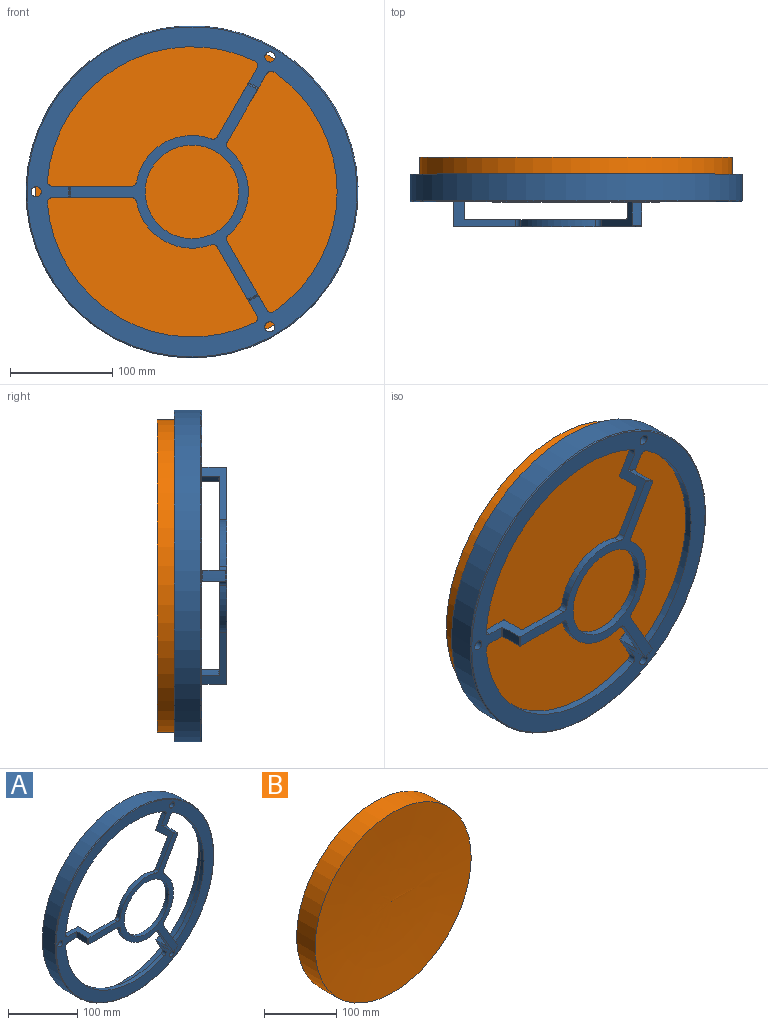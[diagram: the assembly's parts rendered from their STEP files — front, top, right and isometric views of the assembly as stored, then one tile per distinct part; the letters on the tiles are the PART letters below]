
ASSEMBLY  parts=2 mates=1
PART A: 54 faces, bbox 351.8x51.5x351.8 mm
  f0: torus R=110.5mm, axis (0,-1,0), area 17.3mm2, adj f1,f14,f34,f49
  f1: cylinder r=109.5mm len=23mm, axis (0,-1,0), area 253.1mm2, adj f0,f2,f34,f49
  f2: torus R=108.5mm, axis (0,-1,0), area 17.3mm2, adj f1,f18,f34,f49
  f3: torus R=118.5mm, axis (0,-1,0), area 17.3mm2, adj f4,f19,f34,f49
  f4: cylinder r=119.5mm len=22.5mm, axis (0,-1,0), area 247.6mm2, adj f3,f5,f34,f49
  f5: torus R=120.5mm, axis (0,-1,0), area 17.3mm2, adj f4,f23,f34,f49
  f6: torus R=110.5mm, axis (0,-1,0), area 17.3mm2, adj f7,f14,f41,f50
  f7: cylinder r=109.5mm len=23mm, axis (0,-1,0), area 253.1mm2, adj f6,f8,f41,f50
  f8: torus R=108.5mm, axis (0,-1,0), area 17.3mm2, adj f7,f18,f41,f50
  f9: torus R=118.5mm, axis (0,-1,0), area 17.3mm2, adj f10,f19,f41,f50
  f10: cylinder r=119.5mm len=22.5mm, axis (0,-1,0), area 247.6mm2, adj f9,f11,f41,f50
  f11: torus R=120.5mm, axis (0,-1,0), area 17.3mm2, adj f10,f23,f41,f50
  f12: plane 325x325mm, normal (0,1,0), area 5026.5mm2, adj f13,f25
  f13: cylinder r=157.5mm len=315mm, axis (0,-1,0), area 19297.2mm2, adj f12,f14
  f14: plane 315x315mm, normal (0,1,0), area 15425.6mm2, adj f0,f6,f13,f15,f30,f31,f32,f33
  f15: torus R=110.5mm, axis (0,-1,0), area 17.3mm2, adj f14,f16,f33,f42
  f16: cylinder r=109.5mm len=23mm, axis (0,-1,0), area 253.1mm2, adj f15,f17,f33,f42
  f17: torus R=108.5mm, axis (0,-1,0), area 17.3mm2, adj f16,f18,f33,f42
  f18: plane 193.19x167.44mm, normal (0,1,0), area 4749.9mm2, adj f2,f8,f17,f26,f27,f28,f29,f33
  f19: plane 210.53x182.45mm, normal (0,-1,0), area 5080.1mm2, adj f3,f9,f20,f26,f27,f28,f29,f33
  f20: torus R=118.5mm, axis (0,-1,0), area 17.3mm2, adj f19,f21,f33,f42
  f21: cylinder r=119.5mm len=22.5mm, axis (0,-1,0), area 247.6mm2, adj f20,f22,f33,f42
  f22: torus R=120.5mm, axis (0,-1,0), area 17.3mm2, adj f21,f23,f33,f42
  f23: plane 323x323mm, normal (0,-1,0), area 19104.1mm2, adj f5,f11,f22,f24,f30,f31,f32,f33
  f24: torus R=161.5mm, axis (0,-1,0), area 1600.2mm2, adj f23,f25
  f25: cylinder r=162.5mm len=325mm, axis (0,-1,0), area 26546.5mm2, adj f12,f24
  f26: cylinder r=45.8mm len=91.6mm, axis (0,-1,0), area 2014.4mm2, adj f18,f19
  f27: cylinder r=5mm len=7mm, axis (0,-1,0), area 48.8mm2, adj f18,f19,f28,f33
  f28: cylinder r=55.15mm len=73.12mm, axis (0,-1,0), area 673.1mm2, adj f18,f19,f27,f29
  f29: cylinder r=5mm len=7mm, axis (0,-1,0), area 48.8mm2, adj f18,f19,f28,f34
  f30: cylinder r=5mm len=7.5mm, axis (0,-1,0), area 61.8mm2, adj f14,f23,f31,f34
  f31: cylinder r=142mm len=202.95mm, axis (0,-1,0), area 2067.1mm2, adj f14,f23,f30,f32
  f32: cylinder r=5mm len=7.5mm, axis (0,-1,0), area 61.8mm2, adj f14,f23,f31,f33
  f33: plane 67.03x38.71mm, normal (-0.87,0,0.5), area 800.5mm2, adj f14,f15,f16,f17,f18,f19,f20,f21
  f34: plane 77.39x32.02mm, normal (0,0,1), area 800.5mm2, adj f0,f1,f2,f3,f4,f5,f14,f18
  f35: cylinder r=5mm len=7mm, axis (0,-1,0), area 48.8mm2, adj f18,f19,f36,f41
  f36: cylinder r=55.15mm len=84.43mm, axis (0,-1,0), area 673.1mm2, adj f18,f19,f35,f37
  f37: cylinder r=5mm len=7mm, axis (0,-1,0), area 48.8mm2, adj f18,f19,f36,f42
  f38: cylinder r=5mm len=7.5mm, axis (0,-1,0), area 61.8mm2, adj f14,f23,f39,f42
  f39: cylinder r=142mm len=234.34mm, axis (0,-1,0), area 2067.1mm2, adj f14,f23,f38,f40
  f40: cylinder r=5mm len=7.5mm, axis (0,-1,0), area 61.8mm2, adj f14,f23,f39,f41
  f41: plane 67.03x38.71mm, normal (0.87,0,0.5), area 800.5mm2, adj f6,f7,f8,f9,f10,f11,f14,f18
  f42: plane 67.03x38.71mm, normal (0.87,0,-0.5), area 800.5mm2, adj f14,f15,f16,f17,f18,f19,f20,f21
  f43: cylinder r=5mm len=7mm, axis (0,-1,0), area 48.8mm2, adj f18,f19,f44,f49
  f44: cylinder r=55.15mm len=73.12mm, axis (0,-1,0), area 673.1mm2, adj f18,f19,f43,f45
  f45: cylinder r=5mm len=7mm, axis (0,-1,0), area 48.8mm2, adj f18,f19,f44,f50
  f46: cylinder r=5mm len=7.5mm, axis (0,-1,0), area 61.8mm2, adj f14,f23,f47,f50
  f47: cylinder r=142mm len=202.95mm, axis (0,-1,0), area 2067.1mm2, adj f14,f23,f46,f48
  f48: cylinder r=5mm len=7.5mm, axis (0,-1,0), area 61.8mm2, adj f14,f23,f47,f49
  f49: plane 77.39x32.02mm, normal (0,0,-1), area 800.5mm2, adj f0,f1,f2,f3,f4,f5,f14,f18
  f50: plane 67.03x38.71mm, normal (-0.87,0,-0.5), area 800.5mm2, adj f6,f7,f8,f9,f10,f11,f14,f18
  f51: cylinder r=5mm len=10mm, axis (0,-1,0), area 235.6mm2, adj f14,f23
  f52: cylinder r=5mm len=10mm, axis (0,-1,0), area 235.6mm2, adj f14,f23
  f53: cylinder r=5mm len=10mm, axis (0,-1,0), area 235.6mm2, adj f14,f23
PART B: 3 faces, bbox 306.3x36x306.3 mm
  f0: cylinder r=153.15mm len=306.3mm, axis (0,1,0), area 34641.7mm2, adj f1,f2
  f1: plane 306.3x306.3mm, normal (0,1,0), area 73685.8mm2, adj f0
  f2: revolved ~306.3x306.3mm, area 73735.3mm2, adj f0
PLACE A at identity
PLACE B rot(axis=(1,0,0),180deg) t=(0,7.5,0)mm
MATE fastened B.f0 <-> A.f0  axis (0,-1,0) through (0,7.5,0)mm
